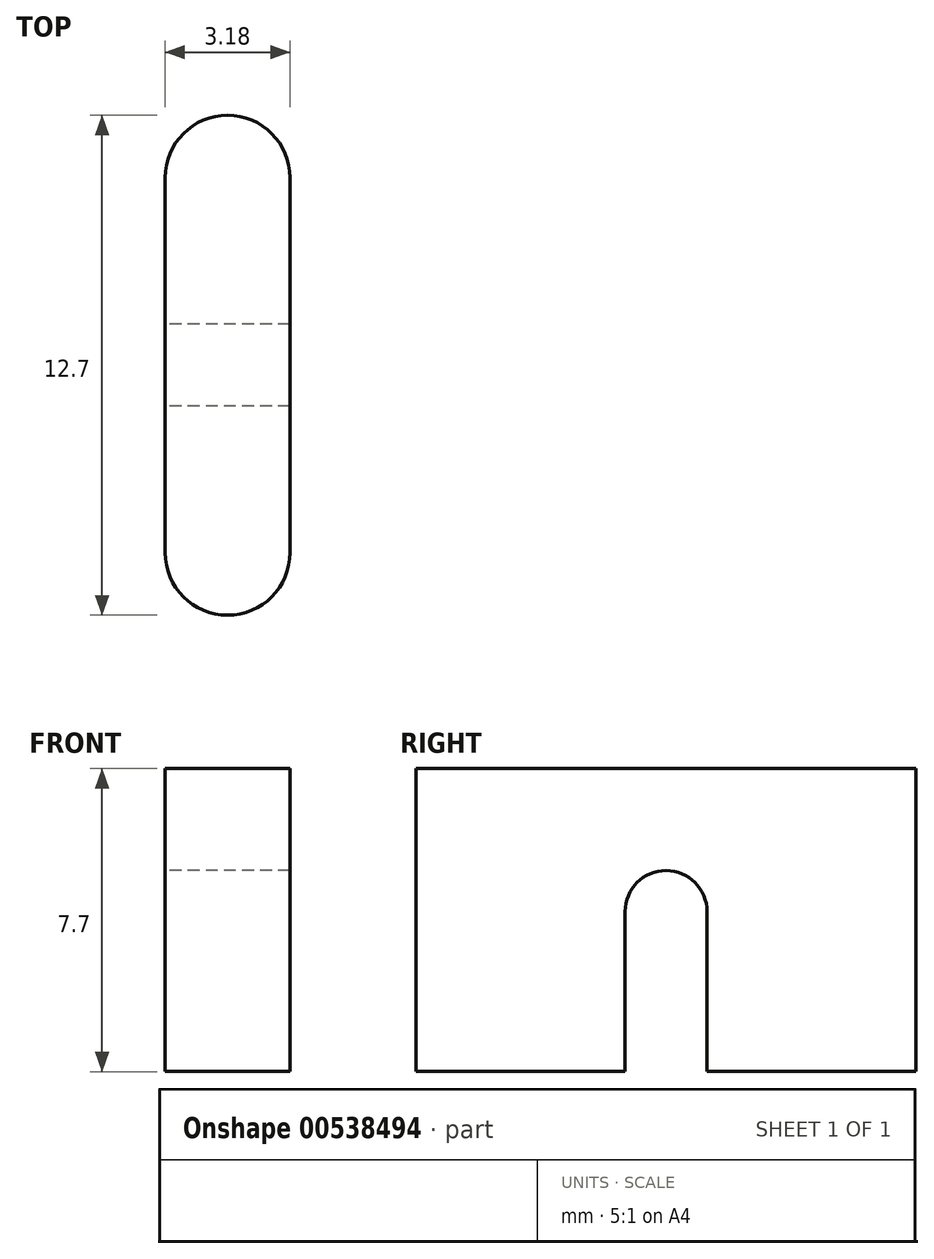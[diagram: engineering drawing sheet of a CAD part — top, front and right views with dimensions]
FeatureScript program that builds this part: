
annotation { "Feature Type Name" : "Feature", "Feature Type Description" : "" }
export const myFeature = defineFeature(function(context is Context, id is Id, definition is map)
    precondition{}
    {
        {
            var Q0;
            Q0=qCreatedBy(makeId("Right.planeOp"),FACE);
            var sketch = newSketch(context, id + "F0", { "sketchPlane" : qUnion([Q0])});
            skLineSegment(sketch, "E0.bottom", {"start": v(-6.35, 3.85) * mm, "end": v(6.35, 3.85) * mm});
            skLineSegment(sketch, "E0.top", {"start": v(-6.35, -3.85) * mm, "end": v(-1.04, -3.85) * mm});
            skLineSegment(sketch, "E0.left", {"start": v(-6.35, 3.85) * mm, "end": v(-6.35, -3.85) * mm});
            skLineSegment(sketch, "E0.right", {"start": v(6.35, 3.85) * mm, "end": v(6.35, -3.85) * mm});
            skArc(sketch, "E1", {"start": v(1.04, 0.22) * mm, "mid": v(0, 1.26) * mm, "end": v(-1.04, 0.22) * mm});
            skPoint(sketch, "E1.centerSnap0", {"position": v(0, -3.85) * mm});
            skLineSegment(sketch, "E2", {"start": v(1.04, 0.22) * mm, "end": v(1.04, -3.85) * mm});
            skLineSegment(sketch, "E3", {"start": v(-1.04, 0.22) * mm, "end": v(-1.04, -3.85) * mm});
            skLineSegment(sketch, "E4.trimOffspring", {"start": v(1.04, -3.85) * mm, "end": v(6.35, -3.85) * mm});
            skSolve(sketch);
        }
        {
            var Q0;
            Q0 = qSketchRegion(id + "F0", true);
            extrude(context, id + "F1", {"entities" : qUnion([Q0]), "endBound" : BoundingType.SYMMETRIC, "depth" : 3.17 * mm, "offsetDistance" : 25.4 * mm});
        }
        {
            var Q0;
            Q0=makeQuery(id+"F1.opExtrude","CAP_EDGE",EDGE,{"disambiguationData":[OSD([sQuery(id+"F0.wireOp",EDGE,"E0.left")])],"isStart":true});
            var Q1;
            Q1=makeQuery(id+"F1.opExtrude","CAP_EDGE",EDGE,{"disambiguationData":[OSD([sQuery(id+"F0.wireOp",EDGE,"E0.left")])],"isStart":false});
            var Q2;
            Q2=makeQuery(id+"F1.opExtrude","CAP_EDGE",EDGE,{"disambiguationData":[OSD([sQuery(id+"F0.wireOp",EDGE,"E0.right")])],"isStart":false});
            var Q3;
            Q3=makeQuery(id+"F1.opExtrude","CAP_EDGE",EDGE,{"disambiguationData":[OSD([sQuery(id+"F0.wireOp",EDGE,"E0.right")])],"isStart":true});
            fillet(context, id + "F2", {"entities" : qUnion([Q0, Q1, Q2, Q3]), "radius" : 1.59 * mm, "tangentPropagation" : true, "allowEdgeOverflow" : false});
        }
    });
